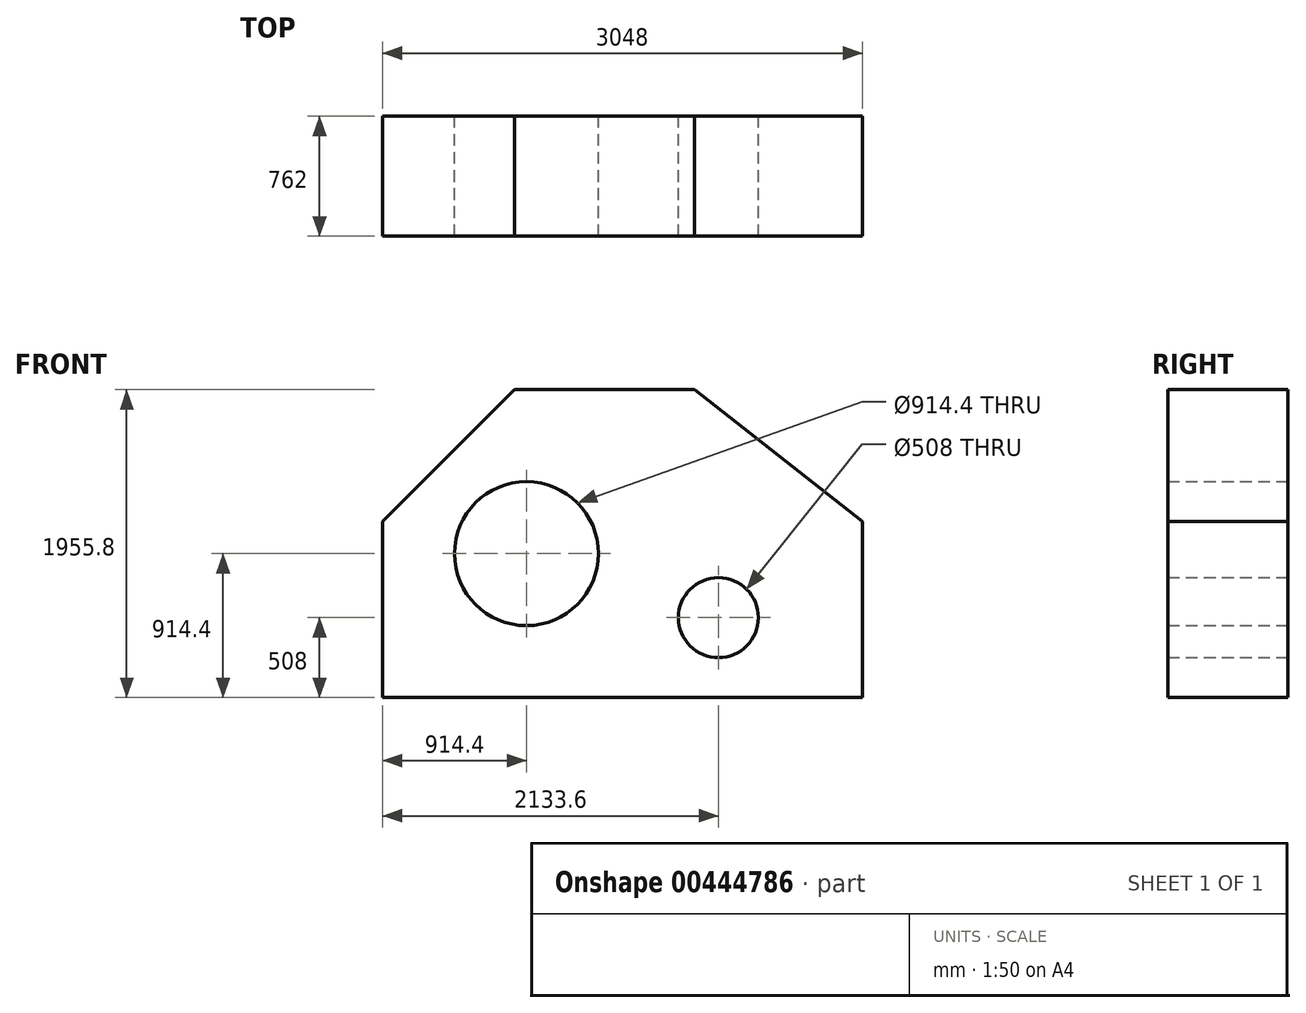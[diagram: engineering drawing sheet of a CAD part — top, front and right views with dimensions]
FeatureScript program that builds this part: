
annotation { "Feature Type Name" : "Feature", "Feature Type Description" : "" }
export const myFeature = defineFeature(function(context is Context, id is Id, definition is map)
    precondition{}
    {
        {
            var Q0;
            Q0=qCreatedBy(makeId("Front.planeOp"),FACE);
            var sketch = newSketch(context, id + "F0", { "sketchPlane" : qUnion([Q0])});
            skLineSegment(sketch, "E0", {"start": v(0, 0) * mm, "end": v(1143, 0) * mm});
            skLineSegment(sketch, "E1", {"start": v(0, 0) * mm, "end": v(-838.2, -838.2) * mm});
            skLineSegment(sketch, "E2", {"start": v(-838.2, -838.2) * mm, "end": v(-838.2, -1955.8) * mm});
            skLineSegment(sketch, "E3", {"start": v(-838.2, -1955.8) * mm, "end": v(2209.8, -1955.8) * mm});
            skLineSegment(sketch, "E4", {"start": v(2209.8, -1955.8) * mm, "end": v(2209.8, -838.2) * mm});
            skLineSegment(sketch, "E5", {"start": v(2209.8, -838.2) * mm, "end": v(1143, 0) * mm});
            skCircle(sketch, "E6", {"center": v(76.2, -1041.4) * mm, "radius": 457.2 * mm});
            skCircle(sketch, "E7", {"center": v(1295.4, -1447.8) * mm, "radius": 254 * mm});
            skPoint(sketch, "E7.centerSnap0", {"position": v(2209.8, -1447.8) * mm});
            skSolve(sketch);
        }
        {
            var Q0;
            Q0=makeQuery(id+"F0.imprint","IMPRINT",FACE,{"disambiguationData":[TD([[makeQuery(id+"F0.imprint","IMPRINT",EDGE,{"derivedFrom":sQuery(id+"F0.wireOp",EDGE,"E0")}),-1.0]])]});
            extrude(context, id + "F1", {"entities" : qUnion([Q0]), "depth" : 762 * mm});
        }
    });
